# Revit family: TechtonicHeadtrack
name_source: partatom
category: Generic Models
units: mm (PartAtom-declared; Revit-internal decimal feet)

## family parameters
Can host rebar = No
Cut with Voids When Loaded = No
Host = Face
OmniClass Number = 23.25.30.24.21
OmniClass Title = Metal Framed Structural Walls
Part Type = Normal
Room Calculation Point = No
Round Connector Dimension = Use Diameter
Shared = No

## types (1)
- TechtonicHeadtrack
    Default Elevation = 1219 mm
    Description = Designed to deal with inter-storey drift and vertifcal deflection between two structures.
    Fire Protection = Passive fire protection systems recommended: RyanFire Batt 502 and FyanFire Graphite Strap.
    IFCExportAs = IfcElementAssembly
    IFCExportType = BRACED_FRAME
    IFCName = Tectonic Headtrack
    Manufacturer = Priest Sheet Metal & Plate
    Masterspec CBI = 3421
    Material = 250MPa, hot dipped galvanised mild steel manufactured in New Zealand.
    Model = Tectonic Headtrack
    Sound Transmission Class = STC 52
    Standard dimension = 2970mm length x  91mm depth. 30mm recessed depth. 1.2mm gauge.
    Tectonic Headtrack Material = Steel Galvanised
    URL = https://www.tris.co.nz

## geometry (parser evidence)
native form markers: Sweep x19
no freeform markers — native parametric forms only
